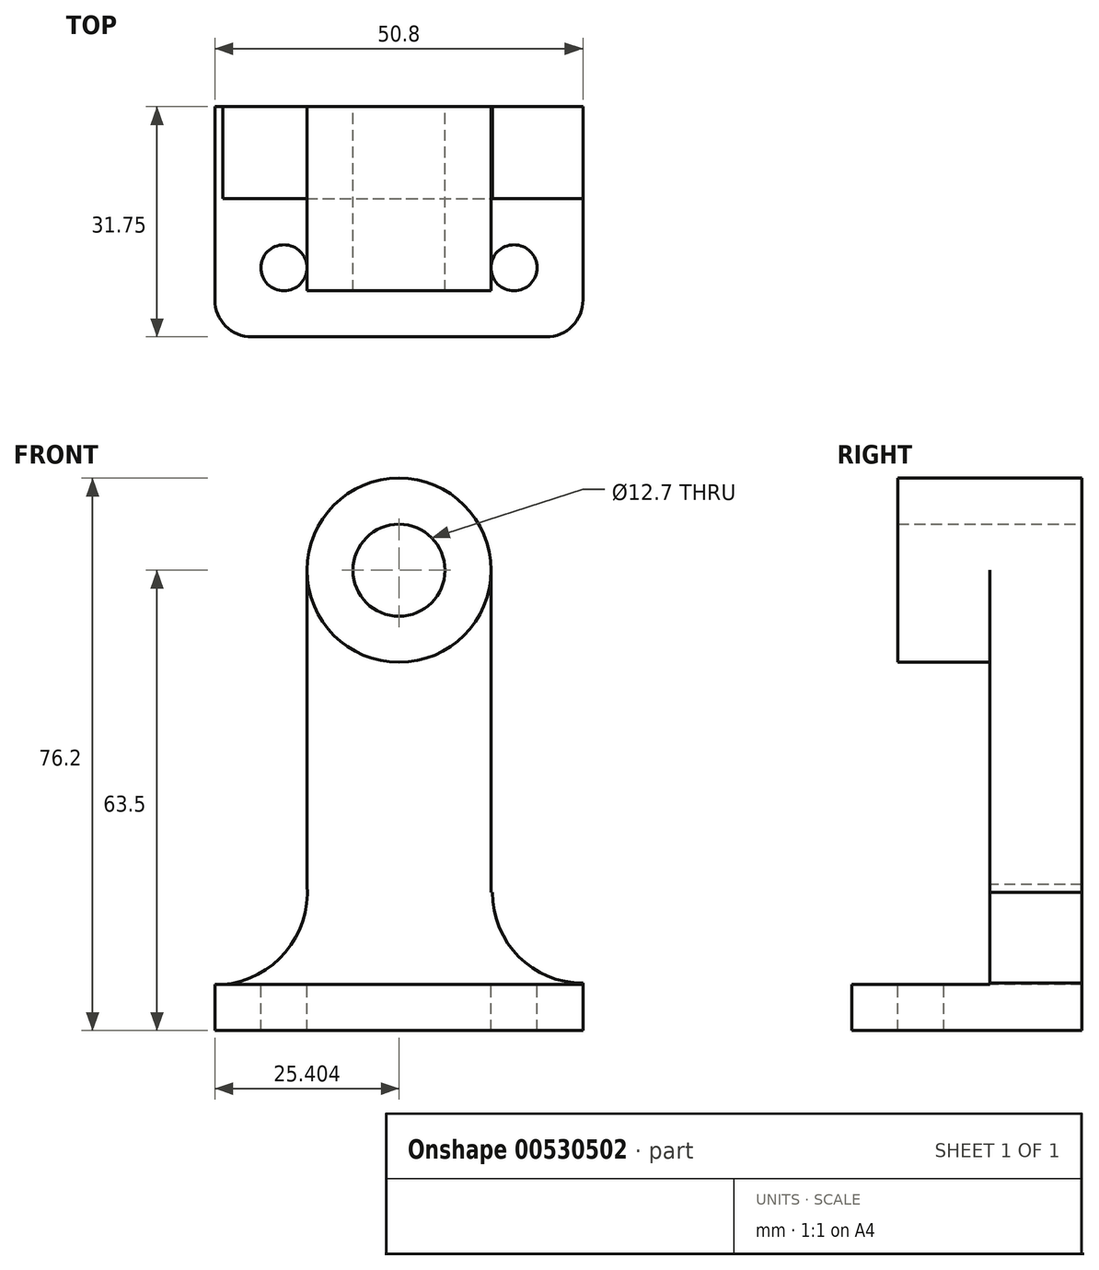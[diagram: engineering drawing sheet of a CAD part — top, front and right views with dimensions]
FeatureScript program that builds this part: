
annotation { "Feature Type Name" : "Feature", "Feature Type Description" : "" }
export const myFeature = defineFeature(function(context is Context, id is Id, definition is map)
    precondition{}
    {
        {
            var Q0;
            Q0=qCreatedBy(makeId("Top.planeOp"),FACE);
            var sketch = newSketch(context, id + "F0", { "sketchPlane" : qUnion([Q0])});
            skLineSegment(sketch, "E0.bottom", {"start": v(-29.9, 31.75) * mm, "end": v(20.9, 31.75) * mm});
            skLineSegment(sketch, "E0.top", {"start": v(-29.9, 0) * mm, "end": v(20.9, 0) * mm});
            skLineSegment(sketch, "E0.left", {"start": v(-29.9, 31.75) * mm, "end": v(-29.9, 0) * mm});
            skLineSegment(sketch, "E0.right", {"start": v(20.9, 31.75) * mm, "end": v(20.9, 0) * mm});
            skSolve(sketch);
        }
        {
            var Q0;
            Q0=makeQuery(id+"F0.imprint","IMPRINT",FACE,{"disambiguationData":[TD([[makeQuery(id+"F0.imprint","IMPRINT",EDGE,{"derivedFrom":sQuery(id+"F0.wireOp",EDGE,"E0.bottom")}),-1.0]])]});
            extrude(context, id + "F1", {"entities" : qUnion([Q0]), "depth" : 6.35 * mm, "offsetDistance" : 25.4 * mm});
        }
        {
            var Q0;
            Q0=makeQuery(id+"F1.opExtrude","CAP_FACE",FACE,{"disambiguationData":[OSD([sQuery(id+"F0.wireOp",EDGE,"E0.bottom"),sQuery(id+"F0.wireOp",EDGE,"E0.top"),sQuery(id+"F0.wireOp",EDGE,"E0.left"),sQuery(id+"F0.wireOp",EDGE,"E0.right")])],"isStart":false});
            var sketch = newSketch(context, id + "F2", { "sketchPlane" : qUnion([Q0])});
            skCircle(sketch, "E1", {"center": v(-20.38, 9.53) * mm, "radius": 3.18 * mm});
            skCircle(sketch, "E2", {"center": v(11.37, 9.53) * mm, "radius": 3.18 * mm});
            skSolve(sketch);
        }
        {
            var Q0;
            Q0=makeQuery(id+"F2.imprint","IMPRINT",FACE,{"disambiguationData":[TD([[makeQuery(id+"F2.imprint","IMPRINT",EDGE,{"derivedFrom":sQuery(id+"F2.wireOp",EDGE,"E2")}),1.0]])]});
            var Q1;
            Q1=makeQuery(id+"F2.imprint","IMPRINT",FACE,{"disambiguationData":[TD([[makeQuery(id+"F2.imprint","IMPRINT",EDGE,{"derivedFrom":sQuery(id+"F2.wireOp",EDGE,"E1")}),1.0]])]});
            extrude(context, id + "F3", {"entities" : qUnion([Q0, Q1]), "operationType" : NewBodyOperationType.REMOVE, "oppositeDirection" : true, "depth" : 25.4 * mm, "offsetDistance" : 25.4 * mm});
        }
        {
            var Q0;
            Q0=makeQuery(id+"F1.opExtrude","SWEPT_EDGE",EDGE,{"disambiguationData":[OSD([sQuery(id+"F0.wireOp",EDGE,"E0.top"),sQuery(id+"F0.wireOp",EDGE,"E0.right")])]});
            var Q1;
            Q1=makeQuery(id+"F1.opExtrude","SWEPT_EDGE",EDGE,{"disambiguationData":[OSD([sQuery(id+"F0.wireOp",EDGE,"E0.top"),sQuery(id+"F0.wireOp",EDGE,"E0.left")])]});
            fillet(context, id + "F4", {"entities" : qUnion([Q0, Q1]), "radius" : 5.08 * mm, "tangentPropagation" : true, "allowEdgeOverflow" : false});
        }
        {
            var Q0;
            Q0=makeQuery(id+"F1.opExtrude","CAP_FACE",FACE,{"disambiguationData":[OSD([sQuery(id+"F0.wireOp",EDGE,"E0.bottom"),sQuery(id+"F0.wireOp",EDGE,"E0.top"),sQuery(id+"F0.wireOp",EDGE,"E0.left"),sQuery(id+"F0.wireOp",EDGE,"E0.right")])],"isStart":false});
            var sketch = newSketch(context, id + "F5", { "sketchPlane" : qUnion([Q0])});
            skLineSegment(sketch, "E3.bottom", {"start": v(-17.2, 31.75) * mm, "end": v(8.2, 31.75) * mm});
            skLineSegment(sketch, "E3.top", {"start": v(-17.2, 19.05) * mm, "end": v(8.2, 19.05) * mm});
            skLineSegment(sketch, "E3.left", {"start": v(-17.2, 31.75) * mm, "end": v(-17.2, 19.05) * mm});
            skLineSegment(sketch, "E3.right", {"start": v(8.2, 31.75) * mm, "end": v(8.2, 19.05) * mm});
            skSolve(sketch);
        }
        {
            var Q0;
            Q0 = qSketchRegion(id + "F5", true);
            extrude(context, id + "F6", {"entities" : qUnion([Q0]), "operationType" : NewBodyOperationType.ADD, "depth" : 69.85 * mm, "offsetDistance" : 25.4 * mm});
        }
        {
            var Q0;
            Q0=makeQuery(id+"F6.opExtrude","SWEPT_FACE",FACE,{"disambiguationData":[OSD([sQuery(id+"F5.wireOp",EDGE,"E3.top")])]});
            var sketch = newSketch(context, id + "F7", { "sketchPlane" : qUnion([Q0])});
            skCircle(sketch, "E4", {"center": v(-4.5, 63.5) * mm, "radius": 6.35 * mm});
            skCircle(sketch, "E5", {"center": v(-4.5, 63.5) * mm, "radius": 12.7 * mm});
            skSolve(sketch);
        }
        {
            var Q0;
            Q0=makeQuery(id+"F7.imprint","IMPRINT",FACE,{"disambiguationData":[TD([[makeQuery(id+"F7.imprint","IMPRINT",EDGE,{"derivedFrom":sQuery(id+"F7.wireOp",EDGE,"E4")}),-1.0]])]});
            extrude(context, id + "F8", {"entities" : qUnion([Q0]), "operationType" : NewBodyOperationType.ADD, "depth" : 12.7 * mm, "offsetDistance" : 25.4 * mm});
        }
        {
            var Q0;
            {var subQ0=sQuery(id+"F5.wireOp",EDGE,"E3.right");var subQ1=sQuery(id+"F5.wireOp",EDGE,"E3.top");var subQ2=makeQuery(id+"F6.opExtrude","SWEPT_FACE",FACE,{"disambiguationData":[OSD([subQ1])]});Q0=makeQuery(id+"F8.boolean.opBoolean","SPLIT",FACE,{"disambiguationData":[TD([makeQuery(id+"F6.opExtrude","CAP_FACE",FACE,{"disambiguationData":[OSD([sQuery(id+"F5.wireOp",EDGE,"E3.bottom"),subQ1,sQuery(id+"F5.wireOp",EDGE,"E3.left"),subQ0])],"isStart":false}),subQ2,makeQuery(id+"F6.opExtrude","SWEPT_FACE",FACE,{"disambiguationData":[OSD([subQ0])]}),makeQuery(id+"F8.opExtrude","SWEPT_FACE",FACE,{"disambiguationData":[OSD([sQuery(id+"F7.wireOp",EDGE,"E5")])]})])],"derivedFrom":subQ2});}
            var Q1;
            {var subQ0=sQuery(id+"F5.wireOp",EDGE,"E3.left");var subQ1=sQuery(id+"F5.wireOp",EDGE,"E3.top");var subQ2=makeQuery(id+"F6.opExtrude","SWEPT_FACE",FACE,{"disambiguationData":[OSD([subQ1])]});Q1=makeQuery(id+"F8.boolean.opBoolean","SPLIT",FACE,{"disambiguationData":[TD([makeQuery(id+"F6.opExtrude","CAP_FACE",FACE,{"disambiguationData":[OSD([sQuery(id+"F5.wireOp",EDGE,"E3.bottom"),subQ1,subQ0,sQuery(id+"F5.wireOp",EDGE,"E3.right")])],"isStart":false}),subQ2,makeQuery(id+"F6.opExtrude","SWEPT_FACE",FACE,{"disambiguationData":[OSD([subQ0])]}),makeQuery(id+"F8.opExtrude","SWEPT_FACE",FACE,{"disambiguationData":[OSD([sQuery(id+"F7.wireOp",EDGE,"E5")])]})])],"derivedFrom":subQ2});}
            var Q2;
            Q2=makeQuery(id+"F8.boolean.opBoolean","SPLIT",FACE,{"disambiguationData":[TD([makeQuery(id+"F8.opExtrude","SWEPT_FACE",FACE,{"disambiguationData":[OSD([sQuery(id+"F7.wireOp",EDGE,"E4")])]})])],"derivedFrom":makeQuery(id+"F6.opExtrude","SWEPT_FACE",FACE,{"disambiguationData":[OSD([sQuery(id+"F5.wireOp",EDGE,"E3.top")])]})});
            extrude(context, id + "F9", {"entities" : qUnion([Q0, Q1, Q2]), "operationType" : NewBodyOperationType.REMOVE, "oppositeDirection" : true, "depth" : 25.4 * mm, "offsetDistance" : 25.4 * mm});
        }
        {
            var Q0;
            Q0=makeQuery(id+"F6.opExtrude","SWEPT_FACE",FACE,{"disambiguationData":[OSD([sQuery(id+"F5.wireOp",EDGE,"E3.right")])]});
            var sketch = newSketch(context, id + "F10", { "sketchPlane" : qUnion([Q0])});
            skLineSegment(sketch, "E6.bottom", {"start": v(19.05, 6.35) * mm, "end": v(31.75, 6.35) * mm});
            skLineSegment(sketch, "E6.top", {"start": v(19.05, 19.05) * mm, "end": v(31.75, 19.05) * mm});
            skLineSegment(sketch, "E6.left", {"start": v(19.05, 6.35) * mm, "end": v(19.05, 19.05) * mm});
            skLineSegment(sketch, "E6.right", {"start": v(31.75, 6.35) * mm, "end": v(31.75, 19.05) * mm});
            skSolve(sketch);
        }
        {
            var Q0;
            Q0=makeQuery(id+"F10.imprint","IMPRINT",FACE,{"disambiguationData":[TD([[makeQuery(id+"F10.imprint","IMPRINT",EDGE,{"derivedFrom":sQuery(id+"F10.wireOp",EDGE,"E6.bottom")}),-1.0]])]});
            extrude(context, id + "F11", {"entities" : qUnion([Q0]), "operationType" : NewBodyOperationType.ADD, "depth" : 12.7 * mm, "offsetDistance" : 25.4 * mm});
        }
        {
            var Q0;
            {var subQ0=makeQuery(id+"F6.opExtrude","SWEPT_FACE",FACE,{"disambiguationData":[OSD([sQuery(id+"F5.wireOp",EDGE,"E3.top")])]});Q0=makeQuery(id+"F11.boolean.opBoolean","MERGE",FACE,{"derivedFrom":[makeQuery(id+"F8.boolean.opBoolean","SPLIT",FACE,{"disambiguationData":[TD([makeQuery(id+"F1.opExtrude","CAP_FACE",FACE,{"disambiguationData":[OSD([sQuery(id+"F0.wireOp",EDGE,"E0.bottom"),sQuery(id+"F0.wireOp",EDGE,"E0.top"),sQuery(id+"F0.wireOp",EDGE,"E0.left"),sQuery(id+"F0.wireOp",EDGE,"E0.right")])],"isStart":false}),subQ0,makeQuery(id+"F6.opExtrude","SWEPT_FACE",FACE,{"disambiguationData":[OSD([sQuery(id+"F5.wireOp",EDGE,"E3.left")])]}),makeQuery(id+"F6.opExtrude","SWEPT_FACE",FACE,{"disambiguationData":[OSD([sQuery(id+"F5.wireOp",EDGE,"E3.right")])]}),makeQuery(id+"F8.opExtrude","SWEPT_FACE",FACE,{"disambiguationData":[OSD([sQuery(id+"F7.wireOp",EDGE,"E5")])]})])],"derivedFrom":subQ0}),makeQuery(id+"F11.opExtrude","SWEPT_FACE",FACE,{"disambiguationData":[OSD([sQuery(id+"F10.wireOp",EDGE,"E6.left")])]})]});}
            var sketch = newSketch(context, id + "F12", { "sketchPlane" : qUnion([Q0])});
            skLineSegment(sketch, "E7", {"start": v(8.2, 19.05) * mm, "end": v(8.2, 6.35) * mm});
            skCircle(sketch, "E8", {"center": v(20.9, 19.05) * mm, "radius": 12.52 * mm});
            skSolve(sketch);
        }
        {
            var Q0;
            {var subQ0=sQuery(id+"F12.wireOp",EDGE,"E8");var subQ1=sQuery(id+"F10.wireOp",EDGE,"E6.left");var subQ4=makeQuery(id+"F11.opExtrude","CAP_EDGE",EDGE,{"disambiguationData":[OSD([subQ1])],"isStart":false});var subQ5=makeQuery(id+"F12.imprint","INTERSECT",VERTEX,{"derivedFrom":[subQ4,subQ0]});Q0=makeQuery(id+"F12.imprint","IMPRINT",FACE,{"disambiguationData":[TD([[makeQuery(id+"F12.imprint","IMPRINT",EDGE,{"disambiguationData":[TD([[subQ5,-1.0]])],"derivedFrom":subQ0}),1.0]])]});}
            var Q1;
            {var subQ0=sQuery(id+"F12.wireOp",EDGE,"E8");var subQ1=sQuery(id+"F10.wireOp",EDGE,"E6.left");var subQ4=makeQuery(id+"F11.opExtrude","CAP_EDGE",EDGE,{"disambiguationData":[OSD([subQ1])],"isStart":false});var subQ5=makeQuery(id+"F12.imprint","INTERSECT",VERTEX,{"derivedFrom":[subQ4,subQ0]});Q1=makeQuery(id+"F12.imprint","IMPRINT",FACE,{"disambiguationData":[TD([[makeQuery(id+"F12.imprint","IMPRINT",EDGE,{"disambiguationData":[TD([[subQ5,1.0]])],"derivedFrom":subQ0}),1.0]])]});}
            extrude(context, id + "F13", {"entities" : qUnion([Q0, Q1]), "operationType" : NewBodyOperationType.REMOVE, "oppositeDirection" : true, "depth" : 25.4 * mm, "offsetDistance" : 25.4 * mm});
        }
        {
            var Q0;
            Q0=makeQuery(id+"F6.opExtrude","SWEPT_FACE",FACE,{"disambiguationData":[OSD([sQuery(id+"F5.wireOp",EDGE,"E3.left")])]});
            var sketch = newSketch(context, id + "F14", { "sketchPlane" : qUnion([Q0])});
            skLineSegment(sketch, "E9.bottom", {"start": v(-31.75, 6.35) * mm, "end": v(-19.05, 6.35) * mm});
            skLineSegment(sketch, "E9.top", {"start": v(-31.75, 19.05) * mm, "end": v(-19.05, 19.05) * mm});
            skLineSegment(sketch, "E9.left", {"start": v(-31.75, 6.35) * mm, "end": v(-31.75, 19.05) * mm});
            skLineSegment(sketch, "E9.right", {"start": v(-19.05, 6.35) * mm, "end": v(-19.05, 19.05) * mm});
            skSolve(sketch);
        }
        {
            var Q0;
            Q0 = qSketchRegion(id + "F14", true);
            extrude(context, id + "F15", {"entities" : qUnion([Q0]), "operationType" : NewBodyOperationType.ADD, "depth" : 12.7 * mm, "offsetDistance" : 25.4 * mm});
        }
        {
            var Q0;
            {var subQ0=makeQuery(id+"F6.opExtrude","SWEPT_FACE",FACE,{"disambiguationData":[OSD([sQuery(id+"F5.wireOp",EDGE,"E3.top")])]});Q0=makeQuery(id+"F15.boolean.opBoolean","MERGE",FACE,{"derivedFrom":[makeQuery(id+"F11.boolean.opBoolean","MERGE",FACE,{"derivedFrom":[makeQuery(id+"F8.boolean.opBoolean","SPLIT",FACE,{"disambiguationData":[TD([makeQuery(id+"F1.opExtrude","CAP_FACE",FACE,{"disambiguationData":[OSD([sQuery(id+"F0.wireOp",EDGE,"E0.bottom"),sQuery(id+"F0.wireOp",EDGE,"E0.top"),sQuery(id+"F0.wireOp",EDGE,"E0.left"),sQuery(id+"F0.wireOp",EDGE,"E0.right")])],"isStart":false}),subQ0,makeQuery(id+"F6.opExtrude","SWEPT_FACE",FACE,{"disambiguationData":[OSD([sQuery(id+"F5.wireOp",EDGE,"E3.left")])]}),makeQuery(id+"F6.opExtrude","SWEPT_FACE",FACE,{"disambiguationData":[OSD([sQuery(id+"F5.wireOp",EDGE,"E3.right")])]}),makeQuery(id+"F8.opExtrude","SWEPT_FACE",FACE,{"disambiguationData":[OSD([sQuery(id+"F7.wireOp",EDGE,"E5")])]})])],"derivedFrom":subQ0}),makeQuery(id+"F11.opExtrude","SWEPT_FACE",FACE,{"disambiguationData":[OSD([sQuery(id+"F10.wireOp",EDGE,"E6.left")])]})]}),makeQuery(id+"F15.opExtrude","SWEPT_FACE",FACE,{"disambiguationData":[OSD([sQuery(id+"F14.wireOp",EDGE,"E9.right")])]})]});}
            var sketch = newSketch(context, id + "F16", { "sketchPlane" : qUnion([Q0])});
            skCircle(sketch, "E10", {"center": v(-29.9, 19.05) * mm, "radius": 12.75 * mm});
            skSolve(sketch);
        }
        {
            var Q0;
            {var subQ0=sQuery(id+"F14.wireOp",EDGE,"E9.right");var subQ3=makeQuery(id+"F15.opExtrude","CAP_EDGE",EDGE,{"disambiguationData":[OSD([subQ0])],"isStart":false});Q0=makeQuery(id+"F16.imprint","IMPRINT",FACE,{"disambiguationData":[TD([[makeQuery(id+"F16.imprint","IMPRINT",EDGE,{"derivedFrom":subQ3}),1.0]])]});}
            extrude(context, id + "F17", {"entities" : qUnion([Q0]), "operationType" : NewBodyOperationType.REMOVE, "oppositeDirection" : true, "depth" : 25.4 * mm, "offsetDistance" : 25.4 * mm});
        }
    });
